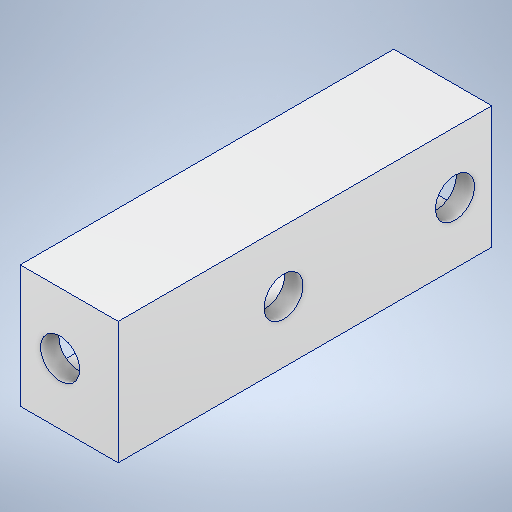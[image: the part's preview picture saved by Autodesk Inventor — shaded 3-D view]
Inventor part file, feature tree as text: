
AUTODESK INVENTOR PART (.ipt)
format: ipt  version: 2025 (Build 290162000, 162)  size: 249,856 bytes
history: native  units: mm
features: sketch x4, projected_geometry x3, extrude x2, hole x2, other x1
ambient origin geometry x8: Origin, YZ Plane, XZ Plane, XY Plane, X Axis, Y Axis, Z Axis, Center Point
bodies: Body1 (feature_tree)
feature tree (12):
  other  "Těleso1"
  extrude  "Vysunutí1"  Depth=8.0mm
  extrude  "Vysunutí2"  Depth=10.0mm
  hole  "Díra1"  [1 undecoded]
  hole  "Díra2"  [1 undecoded]
  sketch  "Náčrt1"
  sketch  "Náčrt2"
  projected_geometry  "Promítnutá smyčka1"
  sketch  "Náčrt3"
  projected_geometry  "Promítnutá smyčka2"
  sketch  "Náčrt4"
  projected_geometry  "Promítnutá smyčka3"
note: 2 required parameter values undecoded (feature->parameter linkage not recoverable at this tier; creation-order binding heuristic only, values carry confidence <= 0.55)
